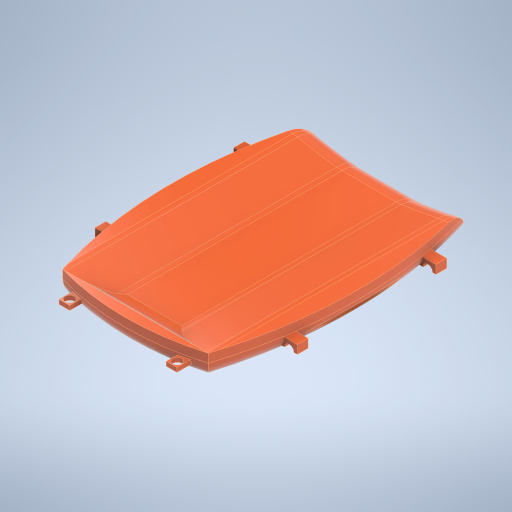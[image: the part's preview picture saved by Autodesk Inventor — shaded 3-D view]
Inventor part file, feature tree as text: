
AUTODESK INVENTOR PART (.ipt)
format: ipt  version: 2023 (Build 270158000, 158)  size: 526,336 bytes
history: native  units: in
note: dims shown in document units (in); Inventor stores cm internally (conversion verified against a paired STEP export)
features: sketch x6, extrude x5, fillet x3, plane x1, hole x1
ambient origin geometry x8: Origin, YZ Plane, XZ Plane, XY Plane, X Axis, Y Axis, Z Axis, Center Point
bodies: Solid1 (feature_tree)
feature tree (16):
  extrude  "Extrusion1"  Depth=2.3622in
  extrude  "Extrusion2"  Depth=3.937in
  fillet  "Fillet2"  Radius=5.4533in
  fillet  "Fillet3"  Radius=1.5748in
  fillet  "Fillet4"  Radius=23.622in
  plane  "Work Plane1"
  sketch  "Sketch4"  dims[d9=39.3701in d10=39.3701in]
  extrude  "Extrusion4"  Depth=39.3701in
  sketch  "Sketch7"  dims[d11=23.622in d12=7.874in]
  extrude  "Extrusion5"  Depth=7.874in
  extrude  "Extrusion6"  Depth=2.3622in TaperAngle=0.0deg
  hole  "Hole4"  [1 undecoded]
  sketch  "Sketch1"  dims[d0=2.3622in d1=2.3622in]
  sketch  "Sketch2"  dims[d2=13.3273in d3=3.937in d5=5.4533in d6=1.5748in d7=23.622in d8=0.0in]
  sketch  "Sketch8"  dims[d13=7.874in d14=2.3622in d15=0.0in]
  sketch  "Sketch10"  dims[d17=2.3622in d18=2.3622in d19=1.5748in d20=-1.1811in d49=0.9843in d50=2.3622in d51=0.0in d52=2.3622in d53=0.9843in d54=2.3622in d55=2.3622in d56=0.7874in d57=0.0in d75=0.876in d76=0.876in d77=17.0in d78=0.0in d79=0.0in d80=0.9843in d81=0.9843in d82=1.5748in d83=1.5748in d84=10.7968in d85=0.3937in d86=0.0in d94=0.876in d95=0.2362in d96=0.1575in d97=0.0787in d98=90.0deg d99=0.315in d100=0.8108in d101=9.8425in d102=1.063in d103=1.063in d16=0.0197in d21=0.0in d22=0.0in d67=0.0394in d68=0.0394in d69=0.0394in d70=0.0059in d71=0.0098in d72=0.0148in d73=0.5635in d74=0.0295in d87=0.0394in d88=0.0394in d89=0.0394in d90=0.0059in d91=0.0098in d92=0.0148in d93=0.5635in d104=0.0295in d105=0.0148in]
note: 1 required parameter value undecoded (feature->parameter linkage not recoverable at this tier; creation-order binding heuristic only, values carry confidence <= 0.55)
